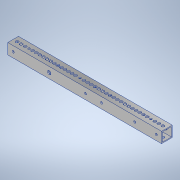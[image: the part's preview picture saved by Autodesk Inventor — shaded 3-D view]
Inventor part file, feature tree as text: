
AUTODESK INVENTOR PART (.ipt)
format: ipt  version: 2020.3 (Build 243373000, 373)  size: 270,336 bytes
history: native  units: mm
features: sketch x9, hole x7, extrude x2, other x1
ambient origin geometry x8: Origin, YZ Plane, XZ Plane, XY Plane, X Axis, Y Axis, Z Axis, Center Point
bodies: Body1 (feature_tree)
feature tree (19):
  other  "ソリッド1"
  extrude  "押し出し1"  Depth=15.0mm
  hole  "穴1"  [1 undecoded]
  hole  "穴2"  [1 undecoded]
  hole  "穴3"  [1 undecoded]
  extrude  "押し出し2"  Depth=1.2mm
  hole  "穴4"  [1 undecoded]
  hole  "穴5"  [1 undecoded]
  hole  "穴6"  [1 undecoded]
  hole  "穴7"  [1 undecoded]
  sketch  "スケッチ1"
  sketch  "スケッチ2"
  sketch  "スケッチ3"
  sketch  "スケッチ4"
  sketch  "スケッチ5"
  sketch  "スケッチ6"
  sketch  "スケッチ7"
  sketch  "スケッチ8"
  sketch  "スケッチ9"
note: 7 required parameter values undecoded (feature->parameter linkage not recoverable at this tier; creation-order binding heuristic only, values carry confidence <= 0.55)
